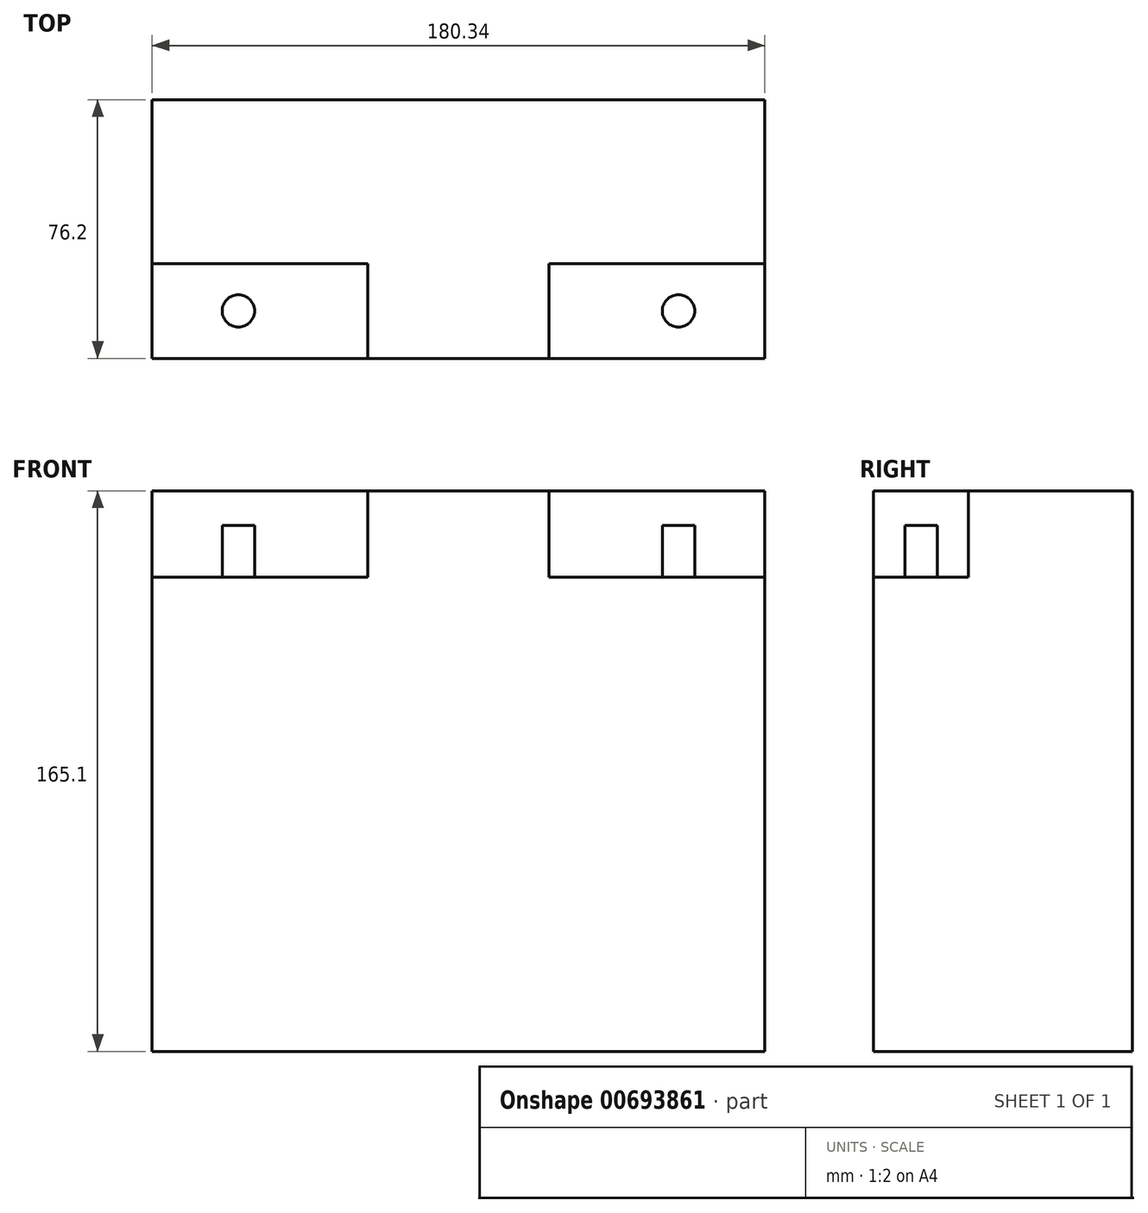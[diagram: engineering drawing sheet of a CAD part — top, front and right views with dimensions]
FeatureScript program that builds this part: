
annotation { "Feature Type Name" : "Feature", "Feature Type Description" : "" }
export const myFeature = defineFeature(function(context is Context, id is Id, definition is map)
    precondition{}
    {
        {
            var Q0;
            Q0=qCreatedBy(makeId("Front.planeOp"),FACE);
            var sketch = newSketch(context, id + "F0", { "sketchPlane" : qUnion([Q0])});
            skLineSegment(sketch, "E0.bottom", {"start": v(0, 0) * mm, "end": v(180.34, 0) * mm});
            skLineSegment(sketch, "E0.top", {"start": v(0, 165.1) * mm, "end": v(180.34, 165.1) * mm});
            skLineSegment(sketch, "E0.left", {"start": v(0, 0) * mm, "end": v(0, 165.1) * mm});
            skLineSegment(sketch, "E0.right", {"start": v(180.34, 0) * mm, "end": v(180.34, 165.1) * mm});
            skSolve(sketch);
        }
        {
            var Q0;
            Q0=makeQuery(id+"F0.imprint","IMPRINT",FACE,{"disambiguationData":[TD([[makeQuery(id+"F0.imprint","IMPRINT",EDGE,{"derivedFrom":sQuery(id+"F0.wireOp",EDGE,"E0.bottom")}),1.0]])]});
            extrude(context, id + "F1", {"entities" : qUnion([Q0]), "depth" : 76.2 * mm, "offsetDistance" : 25.4 * mm});
        }
        {
            var Q0;
            Q0=makeQuery(id+"F1.opExtrude","SWEPT_FACE",FACE,{"disambiguationData":[OSD([sQuery(id+"F0.wireOp",EDGE,"E0.top")])]});
            var sketch = newSketch(context, id + "F2", { "sketchPlane" : qUnion([Q0])});
            skLineSegment(sketch, "E1.bottom", {"start": v(0, -76.2) * mm, "end": v(63.5, -76.2) * mm});
            skLineSegment(sketch, "E1.top", {"start": v(0, -48.26) * mm, "end": v(63.5, -48.26) * mm});
            skLineSegment(sketch, "E1.left", {"start": v(0, -76.2) * mm, "end": v(0, -48.26) * mm});
            skLineSegment(sketch, "E1.right", {"start": v(63.5, -76.2) * mm, "end": v(63.5, -48.26) * mm});
            skSolve(sketch);
        }
        {
            var Q0;
            Q0=makeQuery(id+"F2.imprint","IMPRINT",FACE,{"disambiguationData":[TD([[makeQuery(id+"F2.imprint","IMPRINT",EDGE,{"derivedFrom":sQuery(id+"F2.wireOp",EDGE,"E1.bottom")}),1.0]])]});
            extrude(context, id + "F3", {"entities" : qUnion([Q0]), "operationType" : NewBodyOperationType.REMOVE, "oppositeDirection" : true, "depth" : 25.4 * mm, "offsetDistance" : 25.4 * mm});
        }
        {
            var Q0;
            Q0=makeQuery(id+"F1.opExtrude","SWEPT_FACE",FACE,{"disambiguationData":[OSD([sQuery(id+"F0.wireOp",EDGE,"E0.top")])]});
            var sketch = newSketch(context, id + "F4", { "sketchPlane" : qUnion([Q0])});
            skSolve(sketch);
        }
        {
            var Q0;
            {var subQ0=sQuery(id+"F0.wireOp",EDGE,"E0.top");Q0=makeQuery(id+"F4.imprint","IMPRINT",FACE,{"disambiguationData":[TD([[makeQuery(id+"F4.imprint","IMPRINT",EDGE,{"derivedFrom":makeQuery(id+"F1.opExtrude","CAP_EDGE",EDGE,{"disambiguationData":[OSD([subQ0])],"isStart":true})}),-1.0]])]});}
            var sketch = newSketch(context, id + "F5", { "sketchPlane" : qUnion([Q0])});
            skLineSegment(sketch, "E2.bottom", {"start": v(180.34, -76.2) * mm, "end": v(116.84, -76.2) * mm});
            skLineSegment(sketch, "E2.top", {"start": v(180.34, -48.26) * mm, "end": v(116.84, -48.26) * mm});
            skLineSegment(sketch, "E2.left", {"start": v(180.34, -76.2) * mm, "end": v(180.34, -48.26) * mm});
            skLineSegment(sketch, "E2.right", {"start": v(116.84, -76.2) * mm, "end": v(116.84, -48.26) * mm});
            skSolve(sketch);
        }
        {
            var Q0;
            Q0=makeQuery(id+"F5.imprint","IMPRINT",FACE,{"disambiguationData":[TD([[makeQuery(id+"F5.imprint","IMPRINT",EDGE,{"derivedFrom":sQuery(id+"F5.wireOp",EDGE,"E2.bottom")}),1.0]])]});
            extrude(context, id + "F6", {"entities" : qUnion([Q0]), "operationType" : NewBodyOperationType.REMOVE, "oppositeDirection" : true, "depth" : 25.4 * mm, "offsetDistance" : 25.4 * mm});
        }
        {
            var Q0;
            Q0=makeQuery(id+"F3.boolean.opBoolean","COPY",FACE,{"derivedFrom":makeQuery(id+"F3.opExtrude","CAP_FACE",FACE,{"disambiguationData":[OSD([sQuery(id+"F2.wireOp",EDGE,"E1.bottom"),sQuery(id+"F2.wireOp",EDGE,"E1.top"),sQuery(id+"F2.wireOp",EDGE,"E1.left"),sQuery(id+"F2.wireOp",EDGE,"E1.right")])],"isStart":false})});
            var sketch = newSketch(context, id + "F7", { "sketchPlane" : qUnion([Q0])});
            skCircle(sketch, "E3", {"center": v(25.4, -62.23) * mm, "radius": 4.76 * mm});
            skSolve(sketch);
        }
        {
            var Q0;
            Q0 = qSketchRegion(id + "F7", true);
            extrude(context, id + "F8", {"entities" : qUnion([Q0]), "operationType" : NewBodyOperationType.ADD, "depth" : 15.24 * mm, "offsetDistance" : 25.4 * mm});
        }
        {
            var Q0;
            Q0=makeQuery(id+"F6.boolean.opBoolean","COPY",FACE,{"derivedFrom":makeQuery(id+"F6.opExtrude","CAP_FACE",FACE,{"disambiguationData":[OSD([sQuery(id+"F5.wireOp",EDGE,"E2.bottom"),sQuery(id+"F5.wireOp",EDGE,"E2.top"),sQuery(id+"F5.wireOp",EDGE,"E2.left"),sQuery(id+"F5.wireOp",EDGE,"E2.right")])],"isStart":false})});
            var sketch = newSketch(context, id + "F9", { "sketchPlane" : qUnion([Q0])});
            skCircle(sketch, "E4", {"center": v(154.94, -62.23) * mm, "radius": 4.76 * mm});
            skPoint(sketch, "E4.centerSnap0", {"position": v(180.34, -62.23) * mm});
            skSolve(sketch);
        }
        {
            var Q0;
            Q0=makeQuery(id+"F9.imprint","IMPRINT",FACE,{"disambiguationData":[TD([[makeQuery(id+"F9.imprint","IMPRINT",EDGE,{"derivedFrom":sQuery(id+"F9.wireOp",EDGE,"E4")}),1.0]])]});
            extrude(context, id + "F10", {"entities" : qUnion([Q0]), "operationType" : NewBodyOperationType.ADD, "depth" : 15.24 * mm, "offsetDistance" : 25.4 * mm});
        }
    });
